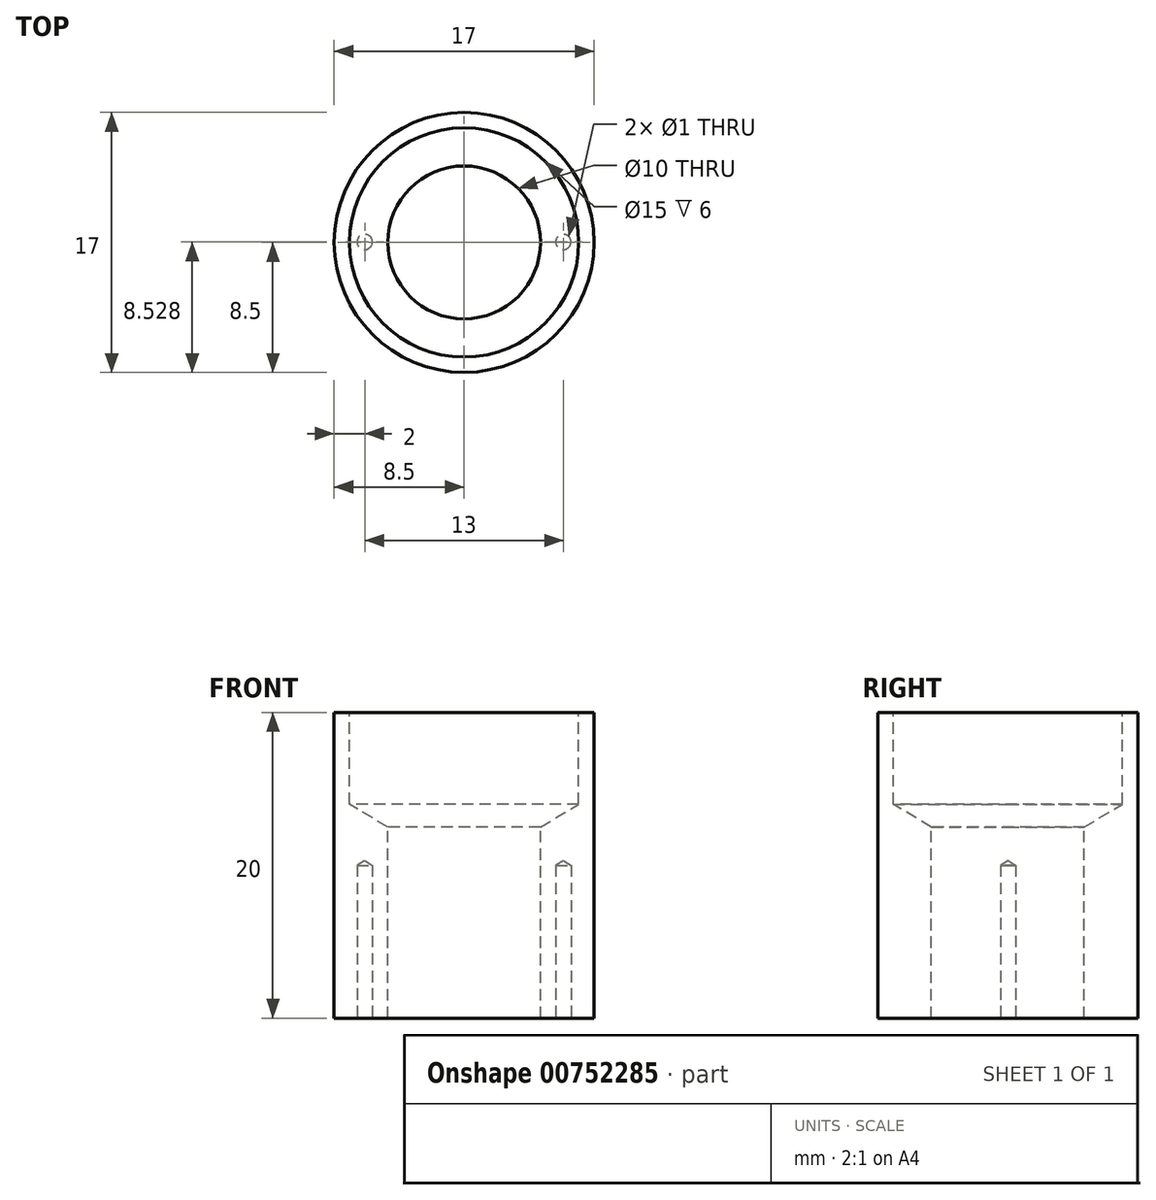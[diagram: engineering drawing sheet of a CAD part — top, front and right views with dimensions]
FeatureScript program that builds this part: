
annotation { "Feature Type Name" : "Feature", "Feature Type Description" : "" }
export const myFeature = defineFeature(function(context is Context, id is Id, definition is map)
    precondition{}
    {
        {
            var Q0;
            Q0=qCreatedBy(makeId("Top.planeOp"),FACE);
            var sketch = newSketch(context, id + "F0", { "sketchPlane" : qUnion([Q0])});
            skCircle(sketch, "E0", {"center": v(0, 0) * mm, "radius": 8.5 * mm});
            skSolve(sketch);
        }
        {
            var Q0;
            Q0=makeQuery(id+"F0.imprint","IMPRINT",FACE,{"disambiguationData":[TD([[makeQuery(id+"F0.imprint","IMPRINT",EDGE,{"derivedFrom":sQuery(id+"F0.wireOp",EDGE,"E0")}),1.0]])]});
            extrude(context, id + "F1", {"entities" : qUnion([Q0]), "depth" : 20 * mm, "offsetDistance" : 25 * mm});
        }
        {
            var Q0;
            Q0=makeQuery(id+"F1.opExtrude","CAP_FACE",FACE,{"disambiguationData":[OSD([sQuery(id+"F0.wireOp",EDGE,"E0")])],"isStart":false});
            var sketch = newSketch(context, id + "F2", { "sketchPlane" : qUnion([Q0])});
            skPoint(sketch, "E1", {"position": v(0, 0) * mm});
            skSolve(sketch);
        }
        {
            var Q0;
            Q0=sQuery(id+"F2.wireOp",VERTEX,"E1");
            var Q1;
            Q1=makeQuery(id+"F1.opExtrude","SWEPT_BODY",BODY,{"disambiguationData":[OSD([sQuery(id+"F0.wireOp",EDGE,"E0")])]});
            hole(context, id + "F3", {"style" : HoleStyle.SIMPLE, "endStyle" : HoleEndStyle.THROUGH, "holeDiameter" : 10 * mm, "majorDiameter" : 5 * mm, "isTappedThrough" : true, "tappedDepth" : 12 * mm, "tapClearance" : 3, "locations" : qUnion([Q0]), "scope" : qUnion([Q1])});
        }
        {
            var Q0;
            Q0=sQuery(id+"F2.wireOp",VERTEX,"E1");
            var Q1;
            Q1=makeQuery(id+"F1.opExtrude","SWEPT_BODY",BODY,{"disambiguationData":[OSD([sQuery(id+"F0.wireOp",EDGE,"E0")])]});
            hole(context, id + "F4", {"style" : HoleStyle.SIMPLE, "endStyle" : HoleEndStyle.BLIND, "holeDiameter" : 15 * mm, "majorDiameter" : 5 * mm, "holeDepth" : 6 * mm, "isTappedThrough" : true, "tappedDepth" : 12 * mm, "tapClearance" : 3, "locations" : qUnion([Q0]), "scope" : qUnion([Q1])});
        }
        {
            var Q0;
            Q0=makeQuery(id+"F1.opExtrude","CAP_FACE",FACE,{"disambiguationData":[OSD([sQuery(id+"F0.wireOp",EDGE,"E0")])],"isStart":true});
            var sketch = newSketch(context, id + "F5", { "sketchPlane" : qUnion([Q0])});
            skPoint(sketch, "E2", {"position": v(6.5, -0.03) * mm});
            skPoint(sketch, "E3", {"position": v(-6.5, -0.03) * mm});
            skSolve(sketch);
        }
        {
            var Q0;
            Q0=sQuery(id+"F5.wireOp",VERTEX,"E3");
            var Q1;
            Q1=sQuery(id+"F5.wireOp",VERTEX,"E2");
            var Q2;
            Q2=makeQuery(id+"F1.opExtrude","SWEPT_BODY",BODY,{"disambiguationData":[OSD([sQuery(id+"F0.wireOp",EDGE,"E0")])]});
            hole(context, id + "F6", {"style" : HoleStyle.SIMPLE, "endStyle" : HoleEndStyle.BLIND, "holeDiameter" : 1 * mm, "majorDiameter" : 5 * mm, "holeDepth" : 10 * mm, "isTappedThrough" : true, "tappedDepth" : 12 * mm, "tapClearance" : 3, "locations" : qUnion([Q0, Q1]), "scope" : qUnion([Q2])});
        }
    });
